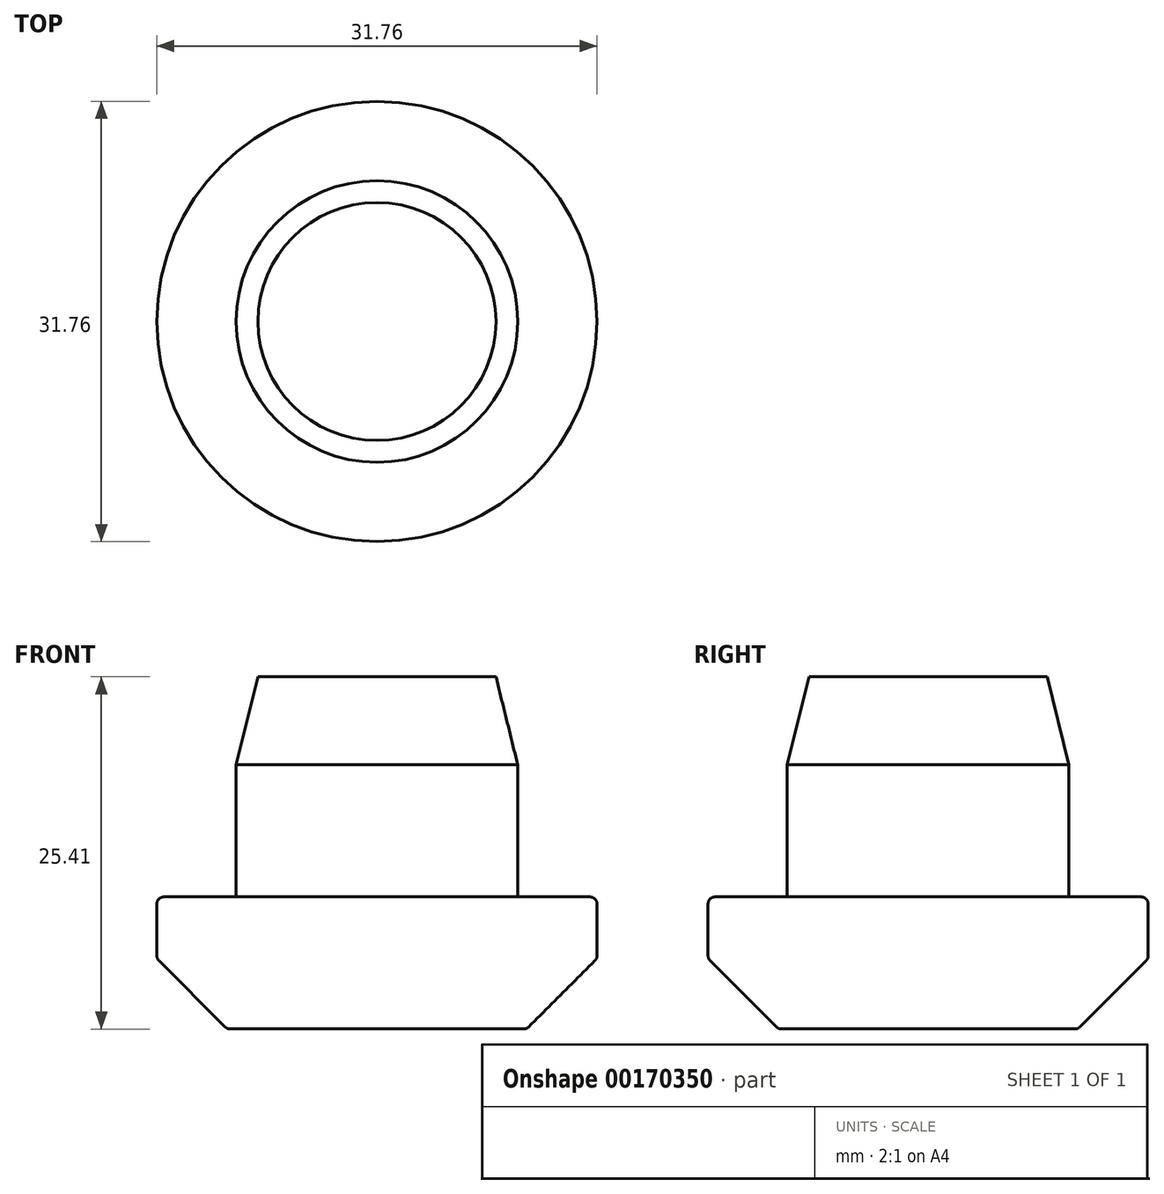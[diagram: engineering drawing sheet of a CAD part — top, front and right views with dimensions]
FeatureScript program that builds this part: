
annotation { "Feature Type Name" : "Feature", "Feature Type Description" : "" }
export const myFeature = defineFeature(function(context is Context, id is Id, definition is map)
    precondition{}
    {
        {
            var Q0;
            Q0=qCreatedBy(makeId("Top.planeOp"),FACE);
            var sketch = newSketch(context, id + "F0", { "sketchPlane" : qUnion([Q0])});
            skCircle(sketch, "E0", {"center": v(0, 0) * mm, "radius": 15.88 * mm});
            skCircle(sketch, "E1", {"center": v(0, 0) * mm, "radius": 10.16 * mm});
            skSolve(sketch);
        }
        {
            var Q0;
            Q0=makeQuery(id+"F0.imprint","IMPRINT",FACE,{"disambiguationData":[TD([[makeQuery(id+"F0.imprint","IMPRINT",EDGE,{"derivedFrom":sQuery(id+"F0.wireOp",EDGE,"E0")}),1.0]])]});
            var Q1;
            Q1=makeQuery(id+"F0.imprint","IMPRINT",FACE,{"disambiguationData":[TD([[makeQuery(id+"F0.imprint","IMPRINT",EDGE,{"derivedFrom":sQuery(id+"F0.wireOp",EDGE,"E1")}),1.0]])]});
            extrude(context, id + "F1", {"entities" : qUnion([Q0, Q1]), "oppositeDirection" : true, "depth" : 9.52 * mm});
        }
        {
            var Q0;
            Q0=makeQuery(id+"F0.imprint","IMPRINT",FACE,{"disambiguationData":[TD([[makeQuery(id+"F0.imprint","IMPRINT",EDGE,{"derivedFrom":sQuery(id+"F0.wireOp",EDGE,"E1")}),1.0]])]});
            extrude(context, id + "F2", {"entities" : qUnion([Q0]), "operationType" : NewBodyOperationType.ADD, "depth" : 15.88 * mm});
        }
        {
            var Q0;
            Q0=makeQuery(id+"F2.opExtrude","CAP_EDGE",EDGE,{"disambiguationData":[OSD([sQuery(id+"F0.wireOp",EDGE,"E1")])],"isStart":false});
            chamfer(context, id + "F3", {"entities" : qUnion([Q0]), "chamferType" : ChamferType.TWO_OFFSETS, "width1" : 6.35 * mm, "oppositeDirection" : true, "width2" : 1.57 * mm, "tangentPropagation" : true});
        }
        {
            var Q0;
            Q0=makeQuery(id+"F1.opExtrude","CAP_EDGE",EDGE,{"disambiguationData":[OSD([sQuery(id+"F0.wireOp",EDGE,"E0")])],"isStart":false});
            chamfer(context, id + "F4", {"entities" : qUnion([Q0]), "width" : 5.08 * mm, "tangentPropagation" : true});
        }
        {
            var Q0;
            Q0=makeQuery(id+"F1.opExtrude","CAP_EDGE",EDGE,{"disambiguationData":[OSD([sQuery(id+"F0.wireOp",EDGE,"E0")])],"isStart":true});
            var Q1;
            {var subQ0=sQuery(id+"F0.wireOp",EDGE,"E0");Q1=makeQuery(id+"F4.opChamfer","BLEND_EDGE",EDGE,{"blendedFrom":[makeQuery(id+"F1.opExtrude","CAP_EDGE",EDGE,{"disambiguationData":[OSD([subQ0])],"isStart":false}),makeQuery(id+"F1.opExtrude","SWEPT_FACE",FACE,{"disambiguationData":[OSD([subQ0])]})],"blendedInto":[makeQuery(id+"F1.opExtrude","SWEPT_FACE",FACE,{"disambiguationData":[OSD([subQ0])]})]});}
            var Q2;
            {var subQ0=sQuery(id+"F0.wireOp",EDGE,"E0");Q2=makeQuery(id+"F4.opChamfer","BLEND_EDGE",EDGE,{"blendedFrom":[makeQuery(id+"F1.opExtrude","CAP_EDGE",EDGE,{"disambiguationData":[OSD([subQ0])],"isStart":false}),makeQuery(id+"F1.opExtrude","CAP_FACE",FACE,{"disambiguationData":[OSD([subQ0])],"isStart":false})],"blendedInto":[makeQuery(id+"F1.opExtrude","CAP_FACE",FACE,{"disambiguationData":[OSD([subQ0])],"isStart":false})]});}
            fillet(context, id + "F5", {"entities" : qUnion([Q0, Q1, Q2]), "radius" : 0.5 * mm, "tangentPropagation" : true, "allowEdgeOverflow" : false});
        }
    });
